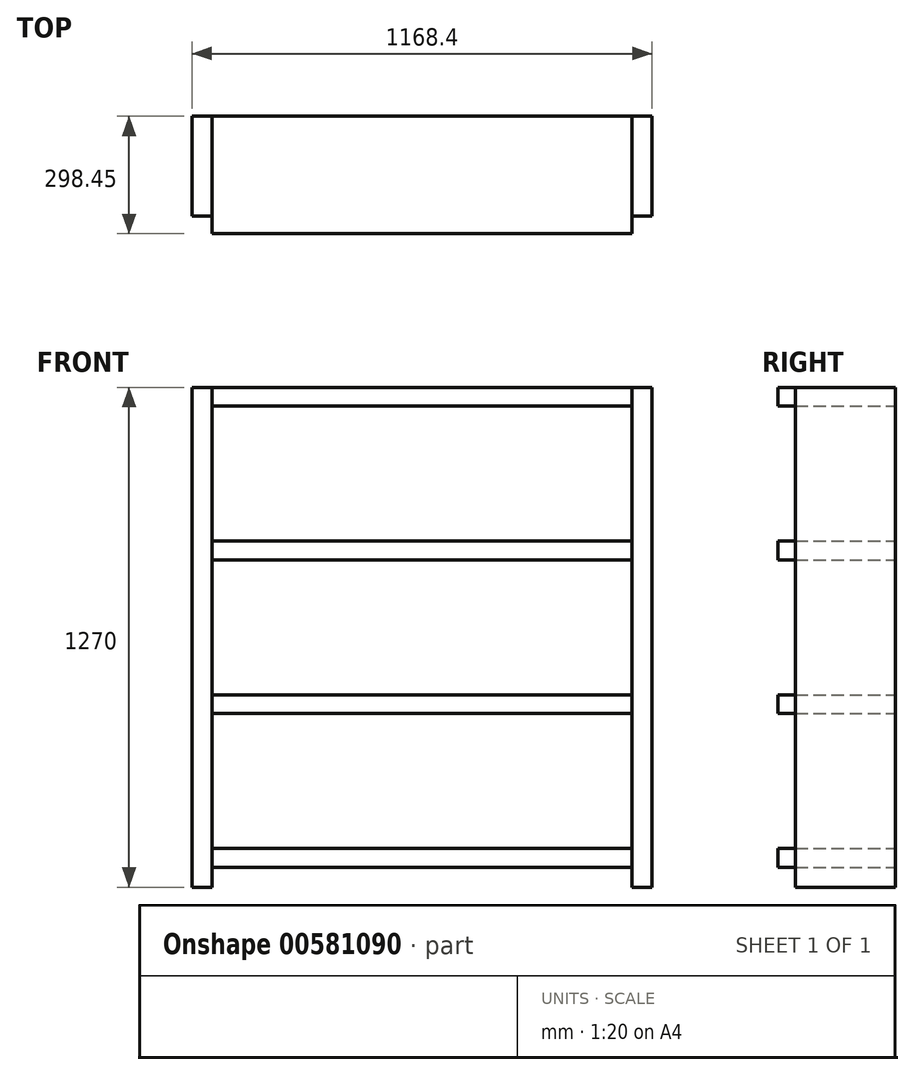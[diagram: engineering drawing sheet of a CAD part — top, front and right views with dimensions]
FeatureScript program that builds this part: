
annotation { "Feature Type Name" : "Feature", "Feature Type Description" : "" }
export const myFeature = defineFeature(function(context is Context, id is Id, definition is map)
    precondition{}
    {
        {
            var Q0;
            Q0=qCreatedBy(makeId("Front.planeOp"),FACE);
            var sketch = newSketch(context, id + "F0", { "sketchPlane" : qUnion([Q0])});
            skLineSegment(sketch, "E0.bottom", {"start": v(0, 1066.8) * mm, "end": v(50.8, 1066.8) * mm});
            skLineSegment(sketch, "E0.top", {"start": v(0, -203.2) * mm, "end": v(50.8, -203.2) * mm});
            skLineSegment(sketch, "E0.left", {"start": v(0, 1066.8) * mm, "end": v(0, -203.2) * mm});
            skLineSegment(sketch, "E0.right", {"start": v(50.8, 1066.8) * mm, "end": v(50.8, -203.2) * mm});
            skPoint(sketch, "E1.firstSnap0", {"position": v(25.4, 1066.8) * mm});
            skLineSegment(sketch, "E1.bottom", {"start": v(1168.4, 1066.8) * mm, "end": v(1117.6, 1066.8) * mm});
            skLineSegment(sketch, "E1.top", {"start": v(1168.4, -203.2) * mm, "end": v(1117.6, -203.2) * mm});
            skLineSegment(sketch, "E1.left", {"start": v(1168.4, 1066.8) * mm, "end": v(1168.4, -203.2) * mm});
            skLineSegment(sketch, "E1.right", {"start": v(1117.6, 1066.8) * mm, "end": v(1117.6, -203.2) * mm});
            skLineSegment(sketch, "E2.bottom", {"start": v(50.8, 285.75) * mm, "end": v(1117.6, 285.75) * mm});
            skLineSegment(sketch, "E2.top", {"start": v(50.8, 238.12) * mm, "end": v(1117.6, 238.12) * mm});
            skLineSegment(sketch, "E2.left", {"start": v(50.8, 285.75) * mm, "end": v(50.8, 238.12) * mm});
            skLineSegment(sketch, "E2.right", {"start": v(1117.6, 285.75) * mm, "end": v(1117.6, 238.12) * mm});
            skLineSegment(sketch, "E3.bottom", {"start": v(50.8, 1066.8) * mm, "end": v(1117.6, 1066.8) * mm});
            skLineSegment(sketch, "E3.top", {"start": v(50.8, 1019.17) * mm, "end": v(1117.6, 1019.17) * mm});
            skLineSegment(sketch, "E3.left", {"start": v(50.8, 1066.8) * mm, "end": v(50.8, 1019.17) * mm});
            skLineSegment(sketch, "E3.right", {"start": v(1117.6, 1066.8) * mm, "end": v(1117.6, 1019.17) * mm});
            skLineSegment(sketch, "E4.bottom", {"start": v(50.8, 676.27) * mm, "end": v(1117.6, 676.27) * mm});
            skLineSegment(sketch, "E4.top", {"start": v(50.8, 628.65) * mm, "end": v(1117.6, 628.65) * mm});
            skLineSegment(sketch, "E4.left", {"start": v(50.8, 676.27) * mm, "end": v(50.8, 628.65) * mm});
            skLineSegment(sketch, "E4.right", {"start": v(1117.6, 676.27) * mm, "end": v(1117.6, 628.65) * mm});
            skLineSegment(sketch, "E5.bottom", {"start": v(50.8, -104.78) * mm, "end": v(1117.6, -104.78) * mm});
            skLineSegment(sketch, "E5.top", {"start": v(50.8, -152.4) * mm, "end": v(1117.6, -152.4) * mm});
            skLineSegment(sketch, "E5.left", {"start": v(50.8, -104.78) * mm, "end": v(50.8, -152.4) * mm});
            skLineSegment(sketch, "E5.right", {"start": v(1117.6, -104.78) * mm, "end": v(1117.6, -152.4) * mm});
            skSolve(sketch);
        }
        {
            var Q0;
            Q0=makeQuery(id+"F0.imprint","IMPRINT",FACE,{"disambiguationData":[TD([[makeQuery(id+"F0.imprint","IMPRINT",EDGE,{"derivedFrom":sQuery(id+"F0.wireOp",EDGE,"E0.bottom")}),-1.0]])]});
            var Q1;
            Q1=makeQuery(id+"F0.imprint","IMPRINT",FACE,{"disambiguationData":[TD([[makeQuery(id+"F0.imprint","IMPRINT",EDGE,{"derivedFrom":sQuery(id+"F0.wireOp",EDGE,"E1.bottom")}),1.0]])]});
            extrude(context, id + "F1", {"entities" : qUnion([Q0, Q1]), "depth" : 254 * mm, "offsetDistance" : 25.4 * mm});
        }
        {
            var Q0;
            Q0=makeQuery(id+"F0.imprint","IMPRINT",FACE,{"disambiguationData":[TD([[makeQuery(id+"F0.imprint","IMPRINT",EDGE,{"derivedFrom":sQuery(id+"F0.wireOp",EDGE,"E3.bottom")}),-1.0]])]});
            var Q1;
            Q1=makeQuery(id+"F0.imprint","IMPRINT",FACE,{"disambiguationData":[TD([[makeQuery(id+"F0.imprint","IMPRINT",EDGE,{"derivedFrom":sQuery(id+"F0.wireOp",EDGE,"E4.bottom")}),-1.0]])]});
            var Q2;
            Q2=makeQuery(id+"F0.imprint","IMPRINT",FACE,{"disambiguationData":[TD([[makeQuery(id+"F0.imprint","IMPRINT",EDGE,{"derivedFrom":sQuery(id+"F0.wireOp",EDGE,"E2.bottom")}),-1.0]])]});
            var Q3;
            Q3=makeQuery(id+"F0.imprint","IMPRINT",FACE,{"disambiguationData":[TD([[makeQuery(id+"F0.imprint","IMPRINT",EDGE,{"derivedFrom":sQuery(id+"F0.wireOp",EDGE,"E5.bottom")}),-1.0]])]});
            extrude(context, id + "F2", {"entities" : qUnion([Q0, Q1, Q2, Q3]), "depth" : 298.45 * mm, "offsetDistance" : 25.4 * mm});
        }
    });
